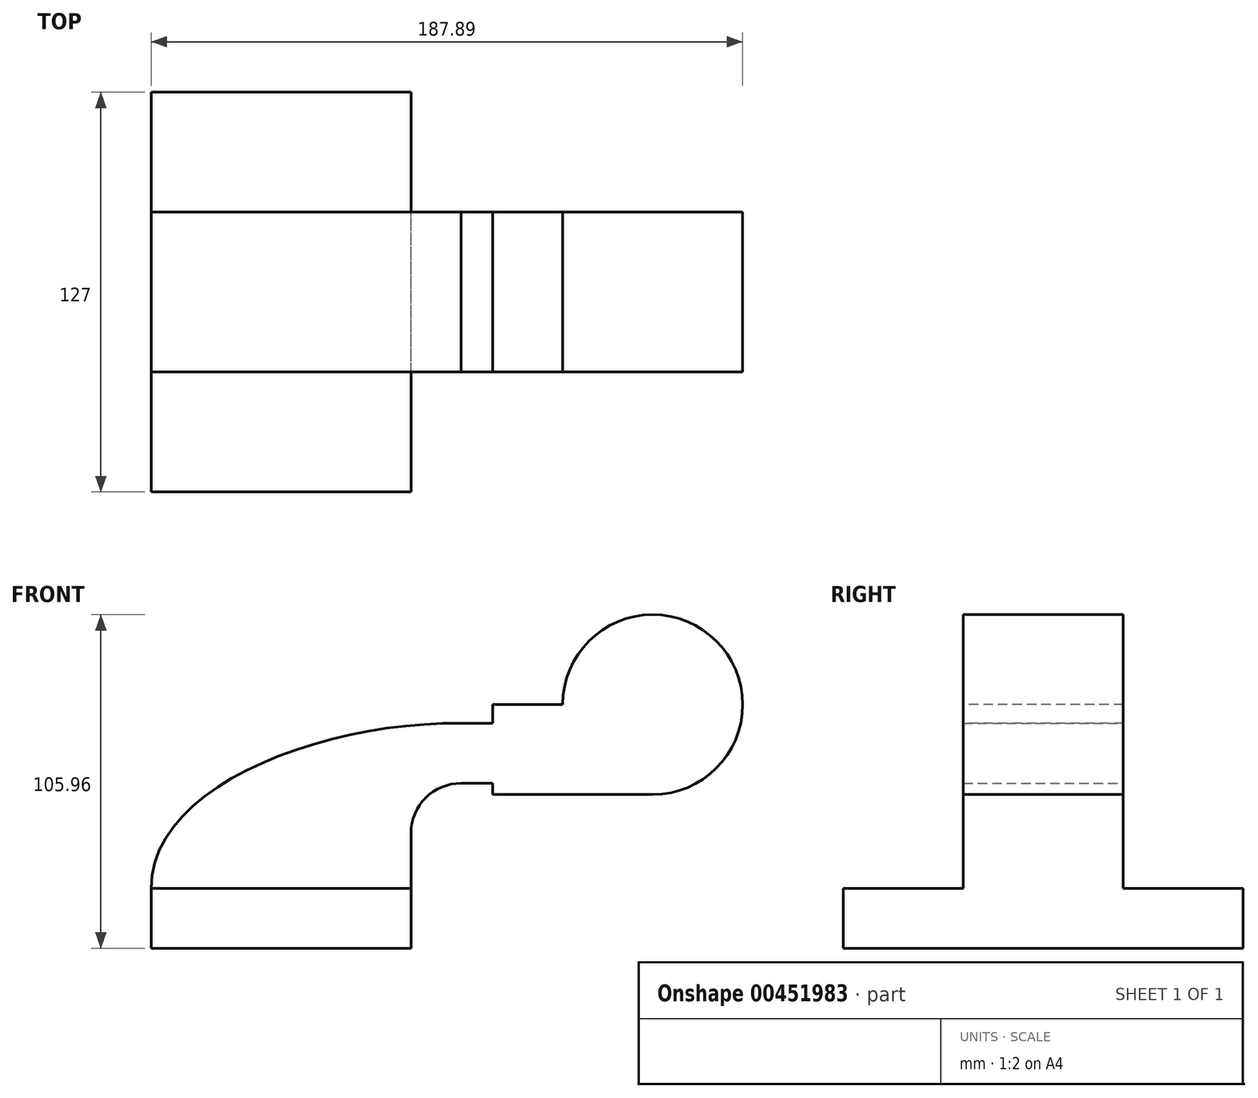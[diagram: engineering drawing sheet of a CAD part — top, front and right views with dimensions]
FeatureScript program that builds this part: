
annotation { "Feature Type Name" : "Feature", "Feature Type Description" : "" }
export const myFeature = defineFeature(function(context is Context, id is Id, definition is map)
    precondition{}
    {
        {
            var Q0;
            Q0=qCreatedBy(makeId("Front.planeOp"),FACE);
            var sketch = newSketch(context, id + "F0", { "sketchPlane" : qUnion([Q0])});
            skLineSegment(sketch, "E0.bottom", {"start": v(-41.28, -9.53) * mm, "end": v(41.28, -9.53) * mm});
            skLineSegment(sketch, "E0.top", {"start": v(-41.28, 9.52) * mm, "end": v(41.28, 9.52) * mm});
            skLineSegment(sketch, "E0.left", {"start": v(-41.28, -9.53) * mm, "end": v(-41.28, 9.53) * mm});
            skLineSegment(sketch, "E0.right", {"start": v(41.28, -9.53) * mm, "end": v(41.28, 9.52) * mm});
            skPoint(sketch, "E0.middle", {"position": v(0, 0) * mm});
            skLineSegment(sketch, "E1.bottom", {"start": v(67.24, 39.28) * mm, "end": v(118.04, 39.28) * mm});
            skLineSegment(sketch, "E1.top", {"start": v(67.24, 67.85) * mm, "end": v(118.04, 67.85) * mm});
            skLineSegment(sketch, "E1.left", {"start": v(67.24, 39.28) * mm, "end": v(67.24, 67.85) * mm});
            skLineSegment(sketch, "E1.right", {"start": v(118.04, 39.28) * mm, "end": v(118.04, 67.85) * mm});
            skPoint(sketch, "E1.middle", {"position": v(92.64, 53.57) * mm});
            skLineSegment(sketch, "E2", {"start": v(41.27, 9.52) * mm, "end": v(41.27, 27) * mm});
            skArc(sketch, "E3", {"start": v(41.27, 27) * mm, "mid": v(45.92, 38.23) * mm, "end": v(57.15, 42.88) * mm});
            skLineSegment(sketch, "E4", {"start": v(57.15, 42.88) * mm, "end": v(93.91, 42.88) * mm});
            skLineSegment(sketch, "E5.0", {"start": v(57.15, 61.93) * mm, "end": v(93.91, 61.93) * mm});
            skArc(sketch, "E5.1", {"start": v(22.23, 27) * mm, "mid": v(32.45, 51.7) * mm, "end": v(57.15, 61.93) * mm});
            skLineSegment(sketch, "E5.2", {"start": v(22.23, 9.52) * mm, "end": v(22.23, 27) * mm});
            skLineSegment(sketch, "E6", {"start": v(93.91, 42.88) * mm, "end": v(93.91, 67.85) * mm});
            skFitSpline(sketch, "E7", {"points": [v(-41.28, 9.53) * mm, v(57.15, 61.93) * mm], "startDerivative": vector(-0.2, 97.48) * mm, "endDerivative": vector(132.3, -1.59) * mm});
            skSolve(sketch);
        }
        {
            var Q0;
            Q0=makeQuery(id+"F0.imprint","IMPRINT",FACE,{"disambiguationData":[TD([[makeQuery(id+"F0.imprint","IMPRINT",EDGE,{"derivedFrom":sQuery(id+"F0.wireOp",EDGE,"E0.bottom")}),1.0]])]});
            extrude(context, id + "F1", {"entities" : qUnion([Q0]), "endBound" : BoundingType.SYMMETRIC, "depth" : 127 * mm});
        }
        {
            var Q0;
            Q0 = qSketchRegion(id + "F0", true);
            extrude(context, id + "F2", {"entities" : qUnion([Q0]), "operationType" : NewBodyOperationType.ADD, "endBound" : BoundingType.SYMMETRIC, "depth" : 50.8 * mm});
        }
        {
            var Q0;
            Q0=makeQuery(id+"F2.opExtrude","SWEPT_FACE",FACE,{"disambiguationData":[OSD([sQuery(id+"F0.wireOp",EDGE,"E1.right")])]});
            var Q1;
            Q1=makeQuery(id+"F2.opExtrude","SWEPT_EDGE",EDGE,{"disambiguationData":[OSD([sQuery(id+"F0.wireOp",EDGE,"E1.top"),sQuery(id+"F0.wireOp",EDGE,"E1.right")])]});
            revolve(context, id + "F3", {"operationType" : NewBodyOperationType.ADD, "entities" : qUnion([Q0]), "axis" : qUnion([Q1]), "revolveType" : RevolveType.FULL});
        }
    });
